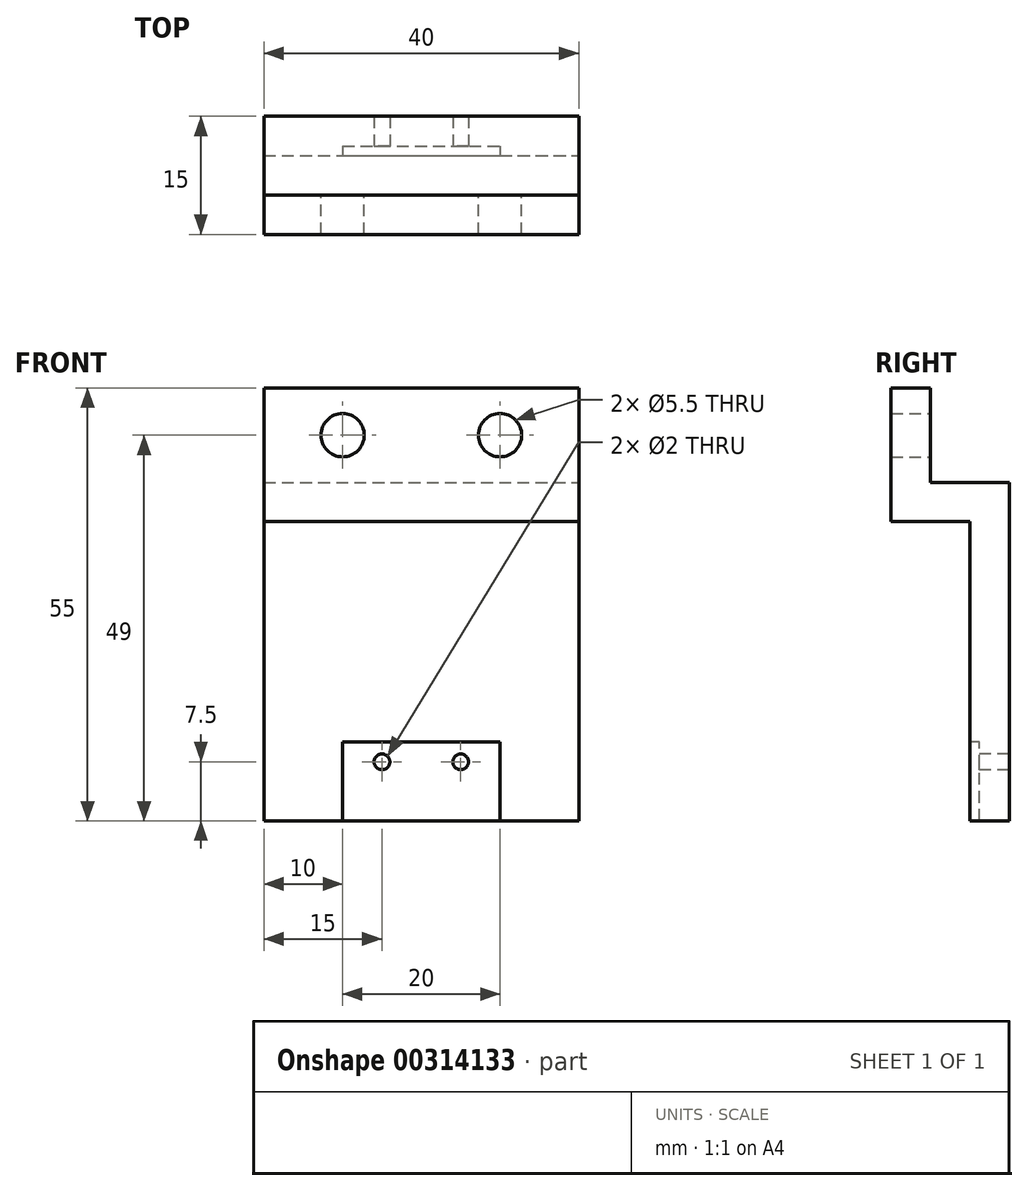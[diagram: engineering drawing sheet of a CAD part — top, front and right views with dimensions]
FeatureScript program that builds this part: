
annotation { "Feature Type Name" : "Feature", "Feature Type Description" : "" }
export const myFeature = defineFeature(function(context is Context, id is Id, definition is map)
    precondition{}
    {
        {
            var Q0;
            Q0=qCreatedBy(makeId("Front.planeOp"),FACE);
            var sketch = newSketch(context, id + "F0", { "sketchPlane" : qUnion([Q0])});
            skLineSegment(sketch, "E0.bottom", {"start": v(0, 0) * mm, "end": v(40, 0) * mm});
            skLineSegment(sketch, "E0.top", {"start": v(0, 12) * mm, "end": v(40, 12) * mm});
            skLineSegment(sketch, "E0.left", {"start": v(0, 0) * mm, "end": v(0, 12) * mm});
            skLineSegment(sketch, "E0.right", {"start": v(40, 0) * mm, "end": v(40, 12) * mm});
            skCircle(sketch, "E1", {"center": v(10, 6) * mm, "radius": 2.75 * mm});
            skPoint(sketch, "E1.centerSnap0", {"position": v(0, 6) * mm});
            skCircle(sketch, "E2", {"center": v(30, 6) * mm, "radius": 2.75 * mm});
            skPoint(sketch, "E2.centerSnap0", {"position": v(40, 6) * mm});
            skSolve(sketch);
        }
        {
            var Q0;
            Q0=makeQuery(id+"F0.imprint","IMPRINT",FACE,{"disambiguationData":[TD([[makeQuery(id+"F0.imprint","IMPRINT",EDGE,{"derivedFrom":sQuery(id+"F0.wireOp",EDGE,"E0.bottom")}),1.0]])]});
            extrude(context, id + "F1", {"entities" : qUnion([Q0]), "depth" : 5 * mm});
        }
        {
            var Q0;
            Q0=makeQuery(id+"F1.opExtrude","SWEPT_FACE",FACE,{"disambiguationData":[OSD([sQuery(id+"F0.wireOp",EDGE,"E0.bottom")])]});
            var sketch = newSketch(context, id + "F2", { "sketchPlane" : qUnion([Q0])});
            skPoint(sketch, "E3.oppositeSnap0", {"position": v(40, 2.5) * mm});
            skLineSegment(sketch, "E3.bottom", {"start": v(0, 5) * mm, "end": v(40, 5) * mm});
            skLineSegment(sketch, "E3.top", {"start": v(0, -10) * mm, "end": v(40, -10) * mm});
            skLineSegment(sketch, "E3.left", {"start": v(0, 5) * mm, "end": v(0, -10) * mm});
            skLineSegment(sketch, "E3.right", {"start": v(40, 5) * mm, "end": v(40, -10) * mm});
            skSolve(sketch);
        }
        {
            var Q0;
            {var subQ0=sQuery(id+"F2.wireOp",EDGE,"E3.top");Q0=makeQuery(id+"F2.imprint","IMPRINT",FACE,{"disambiguationData":[TD([[makeQuery(id+"F2.imprint","IMPRINT",EDGE,{"derivedFrom":subQ0}),1.0]])]});}
            var Q1;
            {var subQ0=sQuery(id+"F2.wireOp",EDGE,"E3.bottom");Q1=makeQuery(id+"F2.imprint","IMPRINT",FACE,{"disambiguationData":[TD([[makeQuery(id+"F2.imprint","IMPRINT",EDGE,{"derivedFrom":subQ0}),-1.0]])]});}
            extrude(context, id + "F3", {"entities" : qUnion([Q0, Q1]), "operationType" : NewBodyOperationType.ADD, "depth" : 5 * mm});
        }
        {
            var Q0;
            Q0=makeQuery(id+"F3.opExtrude","CAP_FACE",FACE,{"disambiguationData":[OSD([sQuery(id+"F2.wireOp",EDGE,"E3.bottom"),sQuery(id+"F2.wireOp",EDGE,"E3.top"),sQuery(id+"F2.wireOp",EDGE,"E3.left"),sQuery(id+"F2.wireOp",EDGE,"E3.right")])],"isStart":false});
            var sketch = newSketch(context, id + "F4", { "sketchPlane" : qUnion([Q0])});
            skLineSegment(sketch, "E4.bottom", {"start": v(0, -10) * mm, "end": v(40, -10) * mm});
            skLineSegment(sketch, "E4.top", {"start": v(0, -5) * mm, "end": v(40, -5) * mm});
            skLineSegment(sketch, "E4.left", {"start": v(0, -10) * mm, "end": v(0, -5) * mm});
            skLineSegment(sketch, "E4.right", {"start": v(40, -10) * mm, "end": v(40, -5) * mm});
            skSolve(sketch);
        }
        {
            var Q0;
            Q0=makeQuery(id+"F4.imprint","IMPRINT",FACE,{"disambiguationData":[TD([[makeQuery(id+"F4.imprint","IMPRINT",EDGE,{"derivedFrom":sQuery(id+"F4.wireOp",EDGE,"E4.bottom")}),1.0]])]});
            extrude(context, id + "F5", {"entities" : qUnion([Q0]), "operationType" : NewBodyOperationType.ADD, "depth" : 38 * mm});
        }
        {
            var Q0;
            Q0=makeQuery(id+"F5.opExtrude","SWEPT_FACE",FACE,{"disambiguationData":[OSD([sQuery(id+"F4.wireOp",EDGE,"E4.top")])]});
            var sketch = newSketch(context, id + "F6", { "sketchPlane" : qUnion([Q0])});
            skLineSegment(sketch, "E5.bottom", {"start": v(10, -43) * mm, "end": v(30, -43) * mm});
            skLineSegment(sketch, "E5.top", {"start": v(10, -33) * mm, "end": v(30, -33) * mm});
            skLineSegment(sketch, "E5.left", {"start": v(10, -43) * mm, "end": v(10, -33) * mm});
            skLineSegment(sketch, "E5.right", {"start": v(30, -43) * mm, "end": v(30, -33) * mm});
            skSolve(sketch);
        }
        {
            var Q0;
            Q0=makeQuery(id+"F6.imprint","IMPRINT",FACE,{"disambiguationData":[TD([[makeQuery(id+"F6.imprint","IMPRINT",EDGE,{"derivedFrom":sQuery(id+"F6.wireOp",EDGE,"E5.bottom")}),1.0]])]});
            extrude(context, id + "F7", {"entities" : qUnion([Q0]), "operationType" : NewBodyOperationType.REMOVE, "oppositeDirection" : true, "depth" : 1.2 * mm});
        }
        {
            var Q0;
            Q0=makeQuery(id+"F7.boolean.opBoolean","COPY",FACE,{"derivedFrom":makeQuery(id+"F7.opExtrude","CAP_FACE",FACE,{"disambiguationData":[OSD([sQuery(id+"F6.wireOp",EDGE,"E5.bottom"),sQuery(id+"F6.wireOp",EDGE,"E5.top"),sQuery(id+"F6.wireOp",EDGE,"E5.left"),sQuery(id+"F6.wireOp",EDGE,"E5.right")])],"isStart":false})});
            var sketch = newSketch(context, id + "F8", { "sketchPlane" : qUnion([Q0])});
            skCircle(sketch, "E6", {"center": v(25, -35.5) * mm, "radius": 1 * mm});
            skCircle(sketch, "E7", {"center": v(15, -35.5) * mm, "radius": 1 * mm});
            skSolve(sketch);
        }
        {
            var Q0;
            Q0=makeQuery(id+"F8.imprint","IMPRINT",FACE,{"disambiguationData":[TD([[makeQuery(id+"F8.imprint","IMPRINT",EDGE,{"derivedFrom":sQuery(id+"F8.wireOp",EDGE,"E7")}),1.0]])]});
            var Q1;
            Q1=makeQuery(id+"F8.imprint","IMPRINT",FACE,{"disambiguationData":[TD([[makeQuery(id+"F8.imprint","IMPRINT",EDGE,{"derivedFrom":sQuery(id+"F8.wireOp",EDGE,"E6")}),1.0]])]});
            extrude(context, id + "F9", {"entities" : qUnion([Q0, Q1]), "operationType" : NewBodyOperationType.REMOVE, "oppositeDirection" : true, "depth" : 25 * mm});
        }
    });
